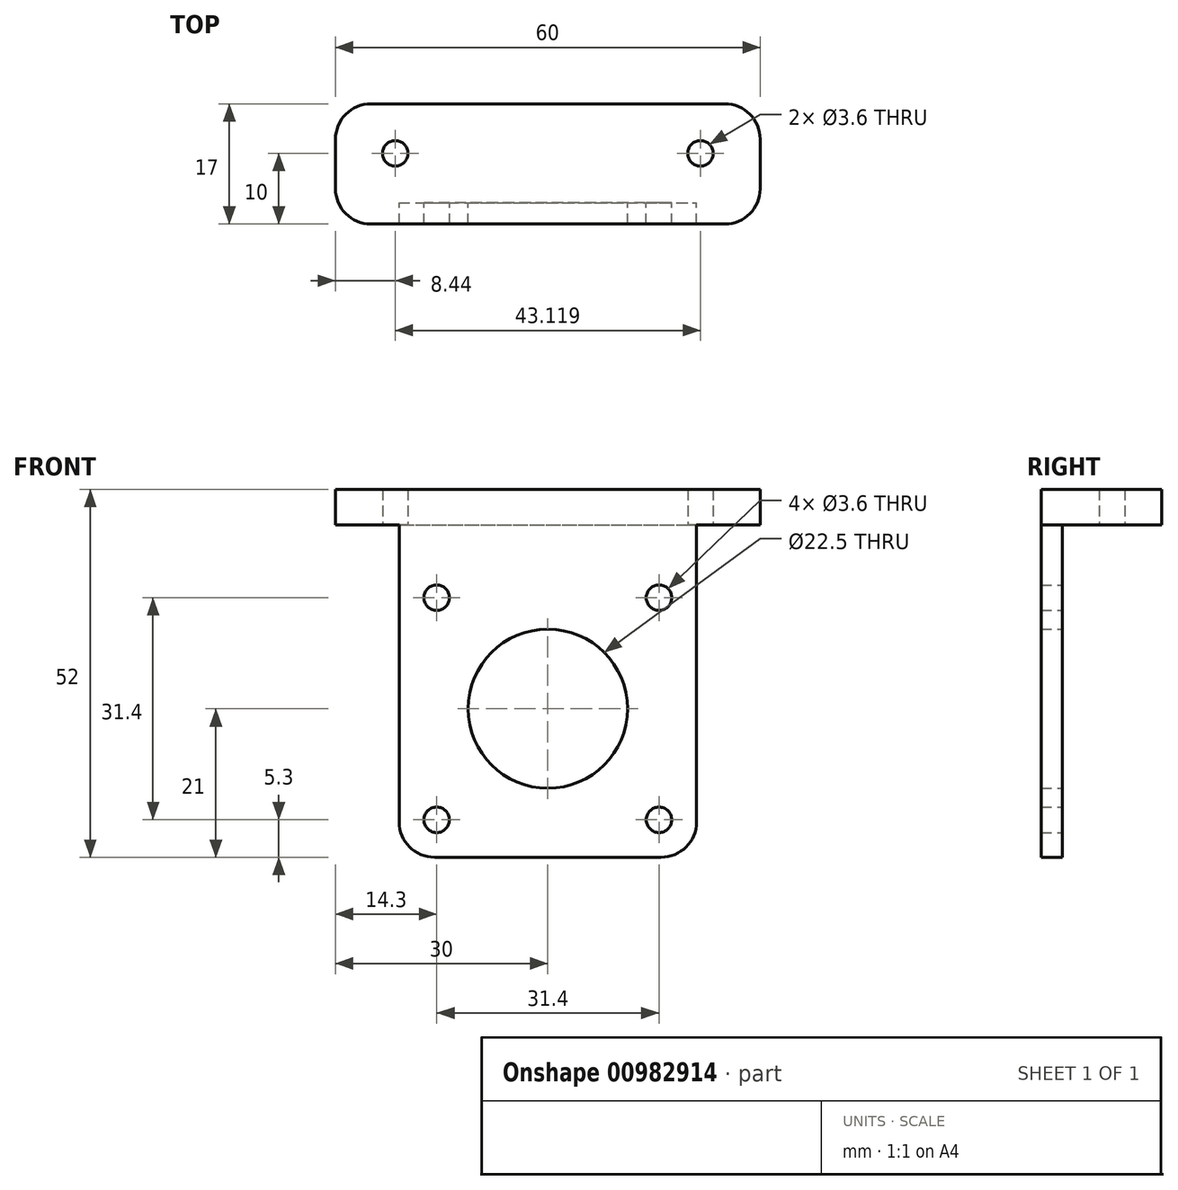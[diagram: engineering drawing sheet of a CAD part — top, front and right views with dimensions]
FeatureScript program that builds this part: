
annotation { "Feature Type Name" : "Feature", "Feature Type Description" : "" }
export const myFeature = defineFeature(function(context is Context, id is Id, definition is map)
    precondition{}
    {
        {
            var Q0;
            Q0=qCreatedBy(makeId("Front.planeOp"),FACE);
            var sketch = newSketch(context, id + "F0", { "sketchPlane" : qUnion([Q0])});
            skLineSegment(sketch, "E0.bottom", {"start": v(21, -21) * mm, "end": v(-21, -21) * mm});
            skLineSegment(sketch, "E0.left", {"start": v(21, -21) * mm, "end": v(21, 21) * mm});
            skLineSegment(sketch, "E0.right", {"start": v(-21, -21) * mm, "end": v(-21, 21) * mm});
            skPoint(sketch, "E0.middle", {"position": v(0, 0) * mm});
            skCircle(sketch, "E1", {"center": v(0, 0) * mm, "radius": 11.25 * mm});
            skCircle(sketch, "E2", {"center": v(-15.7, 15.7) * mm, "radius": 1.8 * mm});
            skCircle(sketch, "E3.MirrorC", {"center": v(15.7, 15.7) * mm, "radius": 1.8 * mm});
            skCircle(sketch, "E4.MirrorC", {"center": v(-15.7, -15.7) * mm, "radius": 1.8 * mm});
            skCircle(sketch, "E5.MirrorC", {"center": v(15.7, -15.7) * mm, "radius": 1.8 * mm});
            skLineSegment(sketch, "E6.top", {"start": v(-21, 31) * mm, "end": v(21, 31) * mm});
            skLineSegment(sketch, "E6.left", {"start": v(-21, 21) * mm, "end": v(-21, 31) * mm});
            skLineSegment(sketch, "E6.right", {"start": v(21, 21) * mm, "end": v(21, 31) * mm});
            skSolve(sketch);
        }
        {
            var Q0;
            Q0=makeQuery(id+"F0.imprint","IMPRINT",FACE,{"disambiguationData":[TD([[makeQuery(id+"F0.imprint","IMPRINT",EDGE,{"derivedFrom":sQuery(id+"F0.wireOp",EDGE,"E0.bottom")}),-1.0]])]});
            extrude(context, id + "F1", {"entities" : qUnion([Q0]), "depth" : 3 * mm, "offsetDistance" : 25 * mm});
        }
        {
            var Q0;
            Q0=makeQuery(id+"F1.opExtrude","CAP_FACE",FACE,{"disambiguationData":[OSD([sQuery(id+"F0.wireOp",EDGE,"E0.bottom"),sQuery(id+"F0.wireOp",EDGE,"E0.left"),sQuery(id+"F0.wireOp",EDGE,"E0.right"),sQuery(id+"F0.wireOp",EDGE,"E1"),sQuery(id+"F0.wireOp",EDGE,"E2"),sQuery(id+"F0.wireOp",EDGE,"E3.MirrorC"),sQuery(id+"F0.wireOp",EDGE,"E4.MirrorC"),sQuery(id+"F0.wireOp",EDGE,"E5.MirrorC"),sQuery(id+"F0.wireOp",EDGE,"E6.top"),sQuery(id+"F0.wireOp",EDGE,"E6.left"),sQuery(id+"F0.wireOp",EDGE,"E6.right")])],"isStart":false});
            var sketch = newSketch(context, id + "F2", { "sketchPlane" : qUnion([Q0])});
            skLineSegment(sketch, "E7.bottom", {"start": v(-30, 31) * mm, "end": v(30, 31) * mm});
            skLineSegment(sketch, "E7.top", {"start": v(-30, 26) * mm, "end": v(30, 26) * mm});
            skLineSegment(sketch, "E7.left", {"start": v(-30, 31) * mm, "end": v(-30, 26) * mm});
            skLineSegment(sketch, "E7.right", {"start": v(30, 31) * mm, "end": v(30, 26) * mm});
            skSolve(sketch);
        }
        {
            var Q0;
            Q0 = qSketchRegion(id + "F2", true);
            extrude(context, id + "F3", {"entities" : qUnion([Q0]), "operationType" : NewBodyOperationType.ADD, "oppositeDirection" : true, "depth" : 17 * mm, "offsetDistance" : 25 * mm});
        }
        {
            var Q0;
            Q0=makeQuery(id+"F3.opExtrude","SWEPT_FACE",FACE,{"disambiguationData":[OSD([sQuery(id+"F2.wireOp",EDGE,"E7.top")])]});
            var sketch = newSketch(context, id + "F4", { "sketchPlane" : qUnion([Q0])});
            skLineSegment(sketch, "E8", {"start": v(-49.65, -7) * mm, "end": v(55.35, -7) * mm, "construction": true});
            skLineSegment(sketch, "E9", {"start": v(0, 30.74) * mm, "end": v(0, -18.55) * mm, "construction": true});
            skPoint(sketch, "E9.endSnap0", {"position": v(0, -14) * mm});
            skCircle(sketch, "E10", {"center": v(-21.56, -7) * mm, "radius": 1.8 * mm});
            skCircle(sketch, "E11", {"center": v(21.56, -7) * mm, "radius": 1.8 * mm});
            skSolve(sketch);
        }
        {
            var Q0;
            Q0 = qSketchRegion(id + "F4", true);
            extrude(context, id + "F5", {"entities" : qUnion([Q0]), "operationType" : NewBodyOperationType.REMOVE, "endBound" : BoundingType.THROUGH_ALL, "oppositeDirection" : true, "depth" : 25 * mm, "offsetDistance" : 25 * mm});
        }
        {
            var Q0;
            Q0=makeQuery(id+"F1.opExtrude","SWEPT_EDGE",EDGE,{"disambiguationData":[OSD([sQuery(id+"F0.wireOp",EDGE,"E0.bottom"),sQuery(id+"F0.wireOp",EDGE,"E0.left")])]});
            var Q1;
            Q1=makeQuery(id+"F1.opExtrude","SWEPT_EDGE",EDGE,{"disambiguationData":[OSD([sQuery(id+"F0.wireOp",EDGE,"E0.bottom"),sQuery(id+"F0.wireOp",EDGE,"E0.right")])]});
            fillet(context, id + "F6", {"entities" : qUnion([Q0, Q1]), "radius" : 5 * mm, "tangentPropagation" : true, "allowEdgeOverflow" : false});
        }
        {
            var Q0;
            Q0=makeQuery(id+"F3.opExtrude","CAP_EDGE",EDGE,{"disambiguationData":[OSD([sQuery(id+"F2.wireOp",EDGE,"E7.left")])],"isStart":true});
            var Q1;
            Q1=makeQuery(id+"F3.opExtrude","CAP_EDGE",EDGE,{"disambiguationData":[OSD([sQuery(id+"F2.wireOp",EDGE,"E7.left")])],"isStart":false});
            var Q2;
            Q2=makeQuery(id+"F3.opExtrude","CAP_EDGE",EDGE,{"disambiguationData":[OSD([sQuery(id+"F2.wireOp",EDGE,"E7.right")])],"isStart":true});
            var Q3;
            Q3=makeQuery(id+"F3.opExtrude","CAP_EDGE",EDGE,{"disambiguationData":[OSD([sQuery(id+"F2.wireOp",EDGE,"E7.right")])],"isStart":false});
            fillet(context, id + "F7", {"entities" : qUnion([Q0, Q1, Q2, Q3]), "radius" : 5 * mm, "tangentPropagation" : true, "allowEdgeOverflow" : false});
        }
    });
